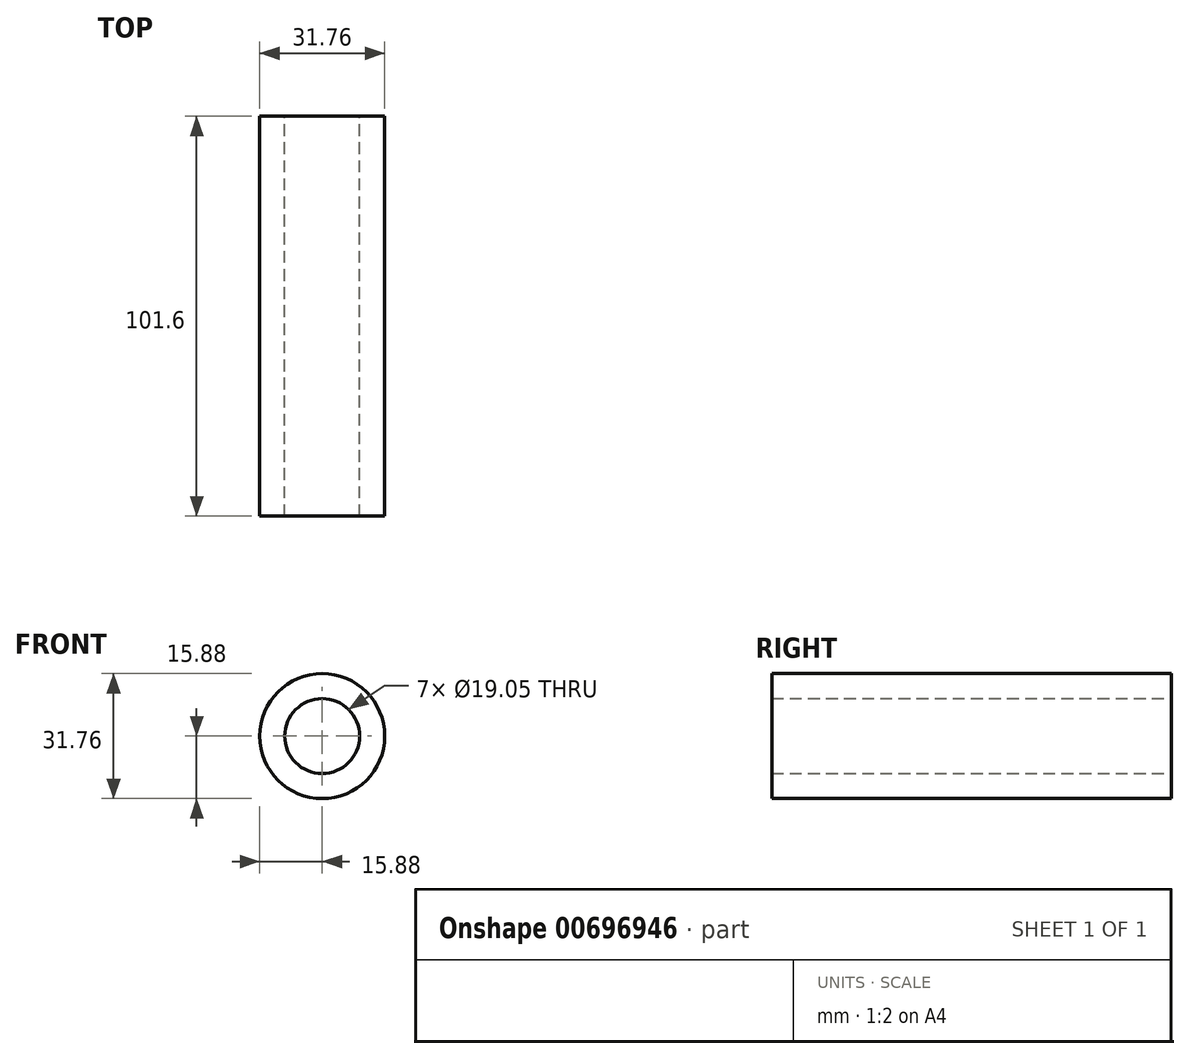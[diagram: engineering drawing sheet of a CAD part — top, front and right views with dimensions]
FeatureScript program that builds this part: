
annotation { "Feature Type Name" : "Feature", "Feature Type Description" : "" }
export const myFeature = defineFeature(function(context is Context, id is Id, definition is map)
    precondition{}
    {
        {
            var Q0;
            Q0=qCreatedBy(makeId("Front.planeOp"),FACE);
            var sketch = newSketch(context, id + "F0", { "sketchPlane" : qUnion([Q0])});
            skCircle(sketch, "E0", {"center": v(0, 0) * mm, "radius": 9.53 * mm});
            skCircle(sketch, "E1", {"center": v(0, 0) * mm, "radius": 15.88 * mm});
            skSolve(sketch);
        }
        {
            var Q0;
            Q0=makeQuery(id+"F0.imprint","IMPRINT",FACE,{"disambiguationData":[TD([[makeQuery(id+"F0.imprint","IMPRINT",EDGE,{"derivedFrom":sQuery(id+"F0.wireOp",EDGE,"E0")}),-1.0]])]});
            extrude(context, id + "F1", {"entities" : qUnion([Q0]), "depth" : 101.6 * mm, "offsetDistance" : 25.4 * mm});
        }
    });
